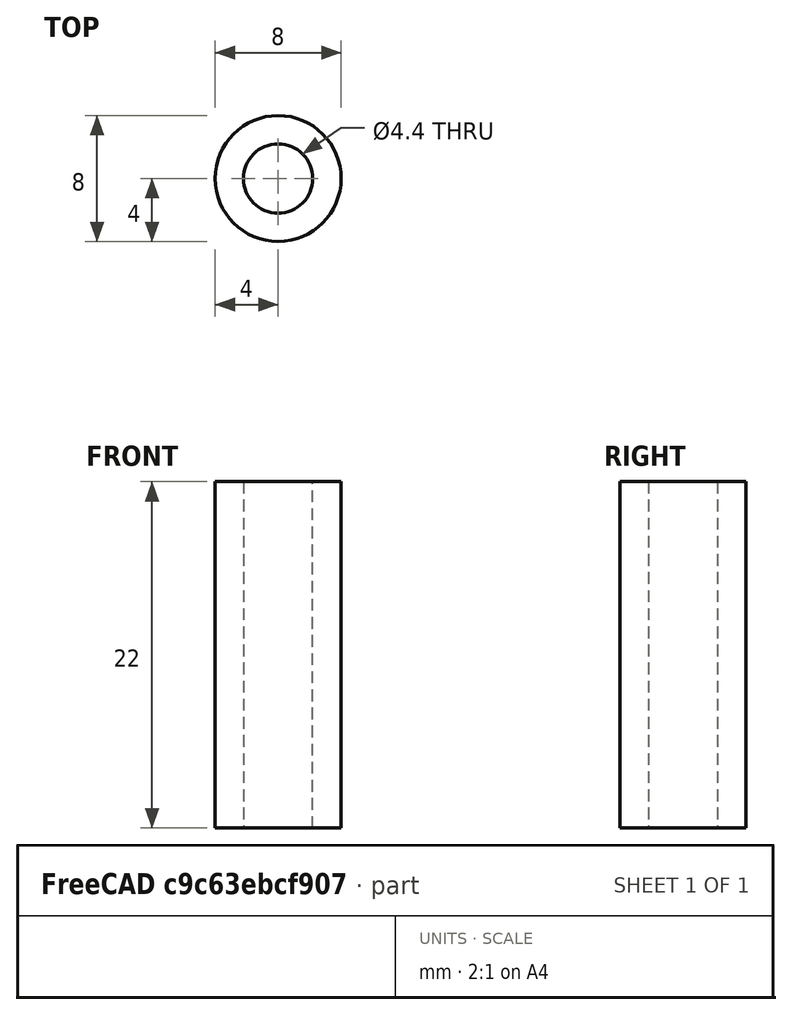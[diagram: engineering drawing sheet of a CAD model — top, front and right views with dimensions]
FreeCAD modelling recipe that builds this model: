
FCSTD DOCUMENT  (FreeCAD 0.18.4R)
Label: for_fixing_drag_chain_on_head
License: All rights reserved
LicenseURL: http://en.wikipedia.org/wiki/All_rights_reserved
objects: Sketcher::SketchObject×1, PartDesign::Pad×1, PartDesign::Body×1
note: 4 computed .brp shape members not serialized (recipe doc carries the construction recipe); baked Part::Feature solids carry a one-line shape summary decoded from their .brp

FEATURE [Sketcher::SketchObject] Sketch
  MapMode = 5
  Support = -> [XY_Plane]
  sketch-geometry (2):
    g0: Circle CenterX=0 CenterY=0 CenterZ=0 NormalX=0 NormalY=0 NormalZ=1 AngleXU=0 Radius=4
    g1: Circle CenterX=0 CenterY=0 CenterZ=0 NormalX=0 NormalY=0 NormalZ=1 AngleXU=0 Radius=2.2
  constraints (4):
    c: Coincident(g0,g-1)
    c: Coincident(g1,g0)
    c: Radius(g1) = 2.2
    c: Radius(g0) = 4
FEATURE [PartDesign::Pad] Pad
  Length = 22
  Length2 = 100
  Profile = -> Sketch
  Type = 0
FEATURE [PartDesign::Body] Body
  Group = -> [Sketch,Pad]
  Origin = -> Origin
  Tip = -> Pad
